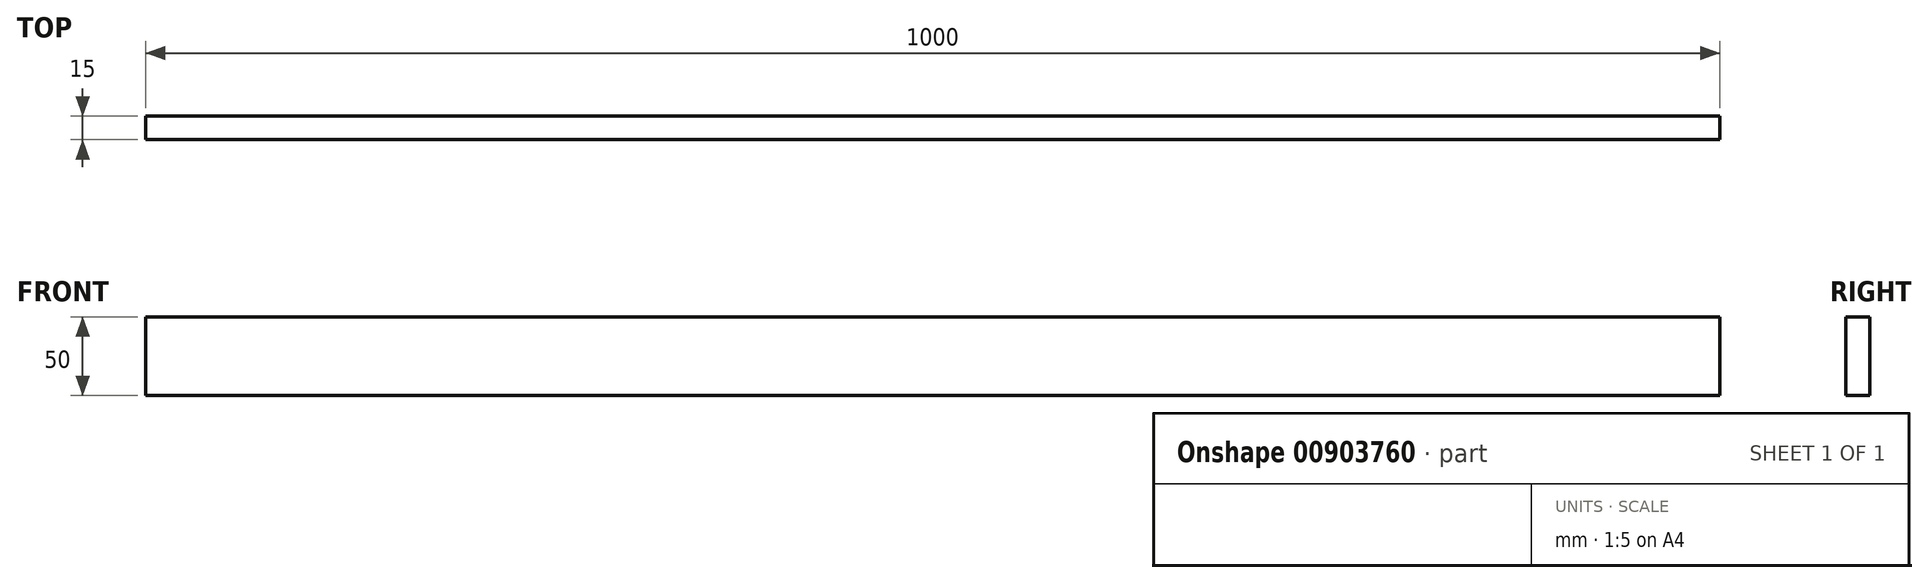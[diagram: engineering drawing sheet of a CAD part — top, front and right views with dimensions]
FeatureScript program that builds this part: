
annotation { "Feature Type Name" : "Feature", "Feature Type Description" : "" }
export const myFeature = defineFeature(function(context is Context, id is Id, definition is map)
    precondition{}
    {
        {
            var Q0;
            Q0=qCreatedBy(makeId("Front.planeOp"),FACE);
            var sketch = newSketch(context, id + "F0", { "sketchPlane" : qUnion([Q0])});
            skLineSegment(sketch, "E0.bottom", {"start": v(-500, 25) * mm, "end": v(500, 25) * mm});
            skLineSegment(sketch, "E0.top", {"start": v(-500, -25) * mm, "end": v(500, -25) * mm});
            skLineSegment(sketch, "E0.left", {"start": v(-500, 25) * mm, "end": v(-500, -25) * mm});
            skLineSegment(sketch, "E0.right", {"start": v(500, 25) * mm, "end": v(500, -25) * mm});
            skSolve(sketch);
        }
        {
            var Q0;
            Q0=makeQuery(id+"F0.imprint","IMPRINT",FACE,{"disambiguationData":[TD([[makeQuery(id+"F0.imprint","IMPRINT",EDGE,{"derivedFrom":sQuery(id+"F0.wireOp",EDGE,"E0.bottom")}),-1.0]])]});
            extrude(context, id + "F1", {"entities" : qUnion([Q0]), "depth" : 15 * mm, "offsetDistance" : 25 * mm});
        }
    });
